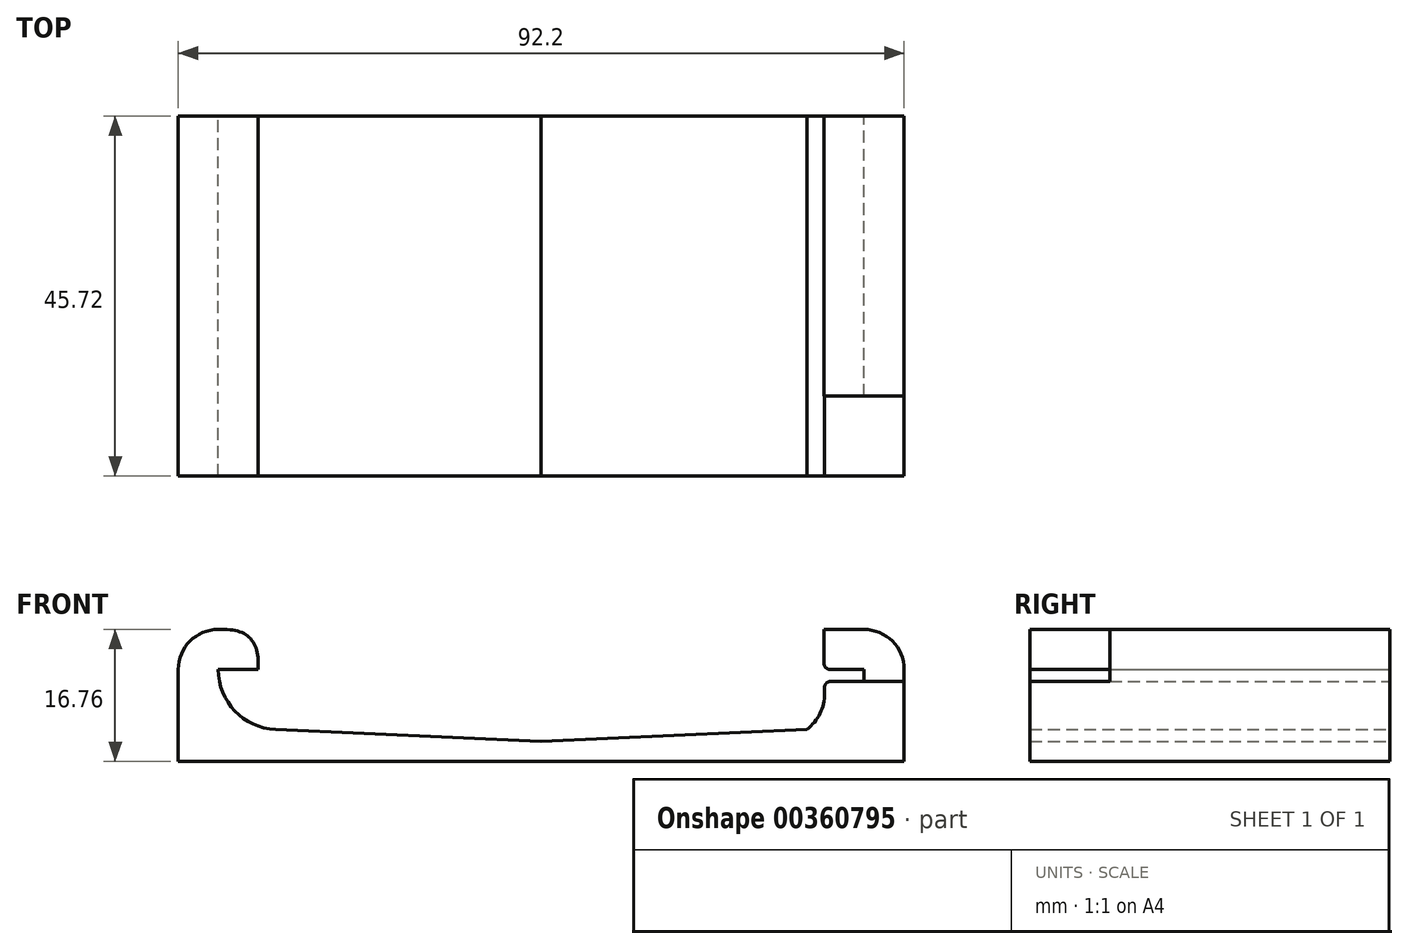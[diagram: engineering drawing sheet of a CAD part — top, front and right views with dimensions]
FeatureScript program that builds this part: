
annotation { "Feature Type Name" : "Feature", "Feature Type Description" : "" }
export const myFeature = defineFeature(function(context is Context, id is Id, definition is map)
    precondition{}
    {
        {
            var Q0;
            Q0=qCreatedBy(makeId("Front.planeOp"),FACE);
            var sketch = newSketch(context, id + "F0", { "sketchPlane" : qUnion([Q0])});
            skLineSegment(sketch, "E0.left", {"start": v(-46.1, 20.96) * mm, "end": v(-46.1, 4.2) * mm});
            skLineSegment(sketch, "E1", {"start": v(-46.1, 20.96) * mm, "end": v(-35.94, 20.96) * mm});
            skLineSegment(sketch, "E2", {"start": v(-35.94, 20.96) * mm, "end": v(-35.94, 15.88) * mm});
            skLineSegment(sketch, "E3", {"start": v(-35.94, 15.88) * mm, "end": v(-41.02, 15.88) * mm});
            skLineSegment(sketch, "E4", {"start": v(-41.02, 15.88) * mm, "end": v(-41.02, 15.88) * mm});
            skLineSegment(sketch, "E5", {"start": v(-33.75, 8.27) * mm, "end": v(0, 6.74) * mm});
            skLineSegment(sketch, "E6", {"start": v(-46.1, 4.2) * mm, "end": v(0, 4.2) * mm});
            skPoint(sketch, "E7.visualSharp", {"position": v(-41.02, 8.6) * mm});
            skArc(sketch, "E7.filletArc", {"start": v(-41.02, 15.88) * mm, "mid": v(-38.9, 10.62) * mm, "end": v(-33.75, 8.27) * mm});
            skLineSegment(sketch, "E8.MirrorCS", {"start": v(41.02, 15.88) * mm, "end": v(41.02, 15.88) * mm});
            skLineSegment(sketch, "E9.MirrorCS", {"start": v(35.94, 20.96) * mm, "end": v(35.94, 15.88) * mm});
            skLineSegment(sketch, "E10.MirrorCS", {"start": v(46.1, 20.96) * mm, "end": v(46.1, 4.2) * mm});
            skLineSegment(sketch, "E11.MirrorCS", {"start": v(46.1, 20.96) * mm, "end": v(35.94, 20.96) * mm});
            skLineSegment(sketch, "E12.MirrorCS", {"start": v(33.75, 8.27) * mm, "end": v(0, 6.74) * mm});
            skPoint(sketch, "E13.MirrorP", {"position": v(41.02, 8.6) * mm});
            skLineSegment(sketch, "E14.MirrorCS", {"start": v(46.1, 4.2) * mm, "end": v(0, 4.2) * mm});
            skLineSegment(sketch, "E15.MirrorCS", {"start": v(35.94, 15.88) * mm, "end": v(41.02, 15.88) * mm});
            skLineSegment(sketch, "E16.top", {"start": v(41.02, 14.36) * mm, "end": v(35.98, 14.36) * mm});
            skLineSegment(sketch, "E16.right", {"start": v(36, 12.85) * mm, "end": v(35.98, 14.36) * mm});
            skLineSegment(sketch, "E17", {"start": v(41.02, 14.36) * mm, "end": v(41.02, 15.88) * mm});
            skArc(sketch, "E18", {"start": v(33.75, 8.27) * mm, "mid": v(35.43, 10.28) * mm, "end": v(36, 12.85) * mm});
            skSolve(sketch);
        }
        {
            var Q0;
            Q0 = qSketchRegion(id + "F0", true);
            extrude(context, id + "F1", {"entities" : qUnion([Q0]), "endBound" : BoundingType.SYMMETRIC, "depth" : 45.72 * mm});
        }
        {
            var Q0;
            Q0=makeQuery(id+"F1.opExtrude","SWEPT_EDGE",EDGE,{"disambiguationData":[OSD([sQuery(id+"F0.wireOp",EDGE,"E0.left"),sQuery(id+"F0.wireOp",EDGE,"E1")])]});
            var Q1;
            Q1=makeQuery(id+"F1.opExtrude","SWEPT_EDGE",EDGE,{"disambiguationData":[OSD([sQuery(id+"F0.wireOp",EDGE,"E10.MirrorCS"),sQuery(id+"F0.wireOp",EDGE,"E11.MirrorCS")])]});
            fillet(context, id + "F2", {"entities" : qUnion([Q0, Q1]), "radius" : 5.08 * mm, "tangentPropagation" : true, "allowEdgeOverflow" : false});
        }
        {
            var Q0;
            Q0=makeQuery(id+"F1.opExtrude","SWEPT_EDGE",EDGE,{"disambiguationData":[OSD([sQuery(id+"F0.wireOp",EDGE,"E16.top"),sQuery(id+"F0.wireOp",EDGE,"E16.right")])]});
            fillet(context, id + "F3", {"entities" : qUnion([Q0]), "radius" : 0.76 * mm, "tangentPropagation" : true, "allowEdgeOverflow" : false});
        }
        {
            var Q0;
            Q0=makeQuery(id+"F1.opExtrude","SWEPT_EDGE",EDGE,{"disambiguationData":[OSD([sQuery(id+"F0.wireOp",EDGE,"E9.MirrorCS"),sQuery(id+"F0.wireOp",EDGE,"E15.MirrorCS")])]});
            fillet(context, id + "F4", {"entities" : qUnion([Q0]), "radius" : 0.76 * mm, "tangentPropagation" : true, "allowEdgeOverflow" : false});
        }
        {
            var Q0;
            Q0=makeQuery(id+"F1.opExtrude","SWEPT_FACE",FACE,{"disambiguationData":[OSD([sQuery(id+"F0.wireOp",EDGE,"E11.MirrorCS")])]});
            var sketch = newSketch(context, id + "F5", { "sketchPlane" : qUnion([Q0])});
            skLineSegment(sketch, "E19.bottom", {"start": v(35.94, -12.7) * mm, "end": v(50.14, -12.7) * mm});
            skLineSegment(sketch, "E19.top", {"start": v(35.94, -22.86) * mm, "end": v(50.14, -22.86) * mm});
            skLineSegment(sketch, "E19.left", {"start": v(35.94, -12.7) * mm, "end": v(35.94, -22.86) * mm});
            skLineSegment(sketch, "E19.right", {"start": v(50.14, -12.7) * mm, "end": v(50.14, -22.86) * mm});
            skSolve(sketch);
        }
        {
            var Q0;
            Q0 = qSketchRegion(id + "F5", true);
            var Q1;
            Q1=makeQuery(id+"F1.opExtrude","SWEPT_FACE",FACE,{"disambiguationData":[OSD([sQuery(id+"F0.wireOp",EDGE,"E16.top")])]});
            extrude(context, id + "F6", {"entities" : qUnion([Q0]), "operationType" : NewBodyOperationType.REMOVE, "endBound" : BoundingType.UP_TO_SURFACE, "oppositeDirection" : true, "endBoundEntityFace" : qUnion([Q1]), "depth" : 25.4 * mm});
        }
        {
            var Q0;
            Q0=makeQuery(id+"F1.opExtrude","SWEPT_EDGE",EDGE,{"disambiguationData":[OSD([sQuery(id+"F0.wireOp",EDGE,"E1"),sQuery(id+"F0.wireOp",EDGE,"E2")])]});
            fillet(context, id + "F7", {"entities" : qUnion([Q0]), "radius" : 4.3 * mm, "tangentPropagation" : true, "rho" : 0.5, "crossSection" : FilletCrossSection.CONIC, "allowEdgeOverflow" : false});
        }
    });
